# Revit family: Lighting_Other_Nordlux_Link_T-Connector_LeftRight
name_source: partatom
category: Lighting Fixtures
revit_build: Autodesk Revit 2017 (Build: 20160225_1515(x64)
units: mm (PartAtom-declared; Revit-internal decimal feet)

## family parameters
Cut with Voids When Loaded = No
Host = Face
Light Source = No
OmniClass Number = 23.80.70.11.14.21
OmniClass Title = Spots and Tracklight Specialties
Part Type = Normal
Room Calculation Point = No
Round Connector Dimension = Use Diameter
Shared = No

## types (2) — shared parameters
AssetType = Fixed
BIMObjectName = Lighting_Other_Nordlux_Link_T-Connector_LeftRight
Brand = Nordlux
Category = Power strip
ConvergoRefNr = 0143-1909-0040-DK
DurationUnit = Year
ElectricalDeviceNominalPower = 0 VA
HasProtectiveEarth = No
IP_Code = IP20
IfcExportAs = IfcLightFixtureType
IfcExportType = NOTDEFINED
InsulationStandardClass = Class 1 (Earth contact)
LightFixtureMountingType = Surface
LightFixturePlacingType = Ceiling
Manufacturer = Nordlux
ManufacturerName = Nordlux
ManufacturerURL = https://www.nordlux.com
Material = Plastic
NBSDescription = Lighting tracks
NBSReference = 90-60-50-430
Name = Nordlux_Link_T-Connector_LeftRight
NominalCurrent = 0 A
NominalDepth = 105 mm
NominalFrequencyRange = 0 Hz
NominalHeight = 18 mm  [stored 0.0590551 ft]
NominalVoltage = 230 V
NominalWidth = 175 mm
NumberOfPoles = 1
PhaseAngle = 0.00°
Product data url = https://www.bimobject.com
Shape = Rectangular
Size = 105x175x18 mm
TotalWattage = 660 W
URL = https://www.nordlux.com
Uniclass2 = Pr_70_70_49_44
Uniclass2015Description = Lighting tracks
Uniclass2015Reference = Pr_70_70_48_47
UsageCurrent = 0 A
Version = 1
VersionDate = 30/08/2019
WarrantyDurationUnit = Year
zero-valued in all types: Default Elevation, MaintenanceFactor, NumberOfSources

## per-type parameters (varying)
| type | ArticleNumber | Color | EAN Number | ModelNumber | RailMainMaterial |
| Link T-connector - black | 86069903 | Black | 5701581402386 | 86069903 | Black |
| Link T-connector - white | 86069901 | White | 5701581402287 | 86069901 | White |

note: column(s) folded — value = type name in every type: Model

note: [stored X ft] marks values corroborated as IEEE doubles in the binary element streams (Revit-internal decimal feet)

## geometry (parser evidence)
native form markers: Sweep x3
no freeform markers — native parametric forms only
